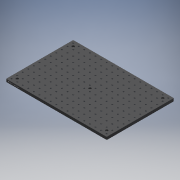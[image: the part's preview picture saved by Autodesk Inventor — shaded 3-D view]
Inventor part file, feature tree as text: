
AUTODESK INVENTOR PART (.ipt)
format: ipt  version: 2019 (Build 230136000, 136)  size: 886,272 bytes
history: mixed  units: in
note: dims shown in document units (in); Inventor stores cm internally (conversion verified against a paired STEP export)
features: extrude x1, sketch x1, projected_geometry x1, other x1, imported_body x1
ambient origin geometry x8: Origin, YZ Plane, XZ Plane, XY Plane, X Axis, Y Axis, Z Axis, Center Point
bodies: Solid1 (imported_parasolid)
feature tree (5):
  extrude  "Extrusion1"  Depth=0.1969in
  sketch  "Sketch1"  dims[d0=0.1969in d1=0.1969in d2=0.1969in d3=0.1969in d4=2.0in d5=0.0in]
  projected_geometry  "Projected Loop1"
  other  "MB1218 - Aluminium Breadboard 304.8 x 457.2 x 12.7mm-1-solid1"
  imported_body  NMx_Import_Brep_tag  [imported B-rep: ~14 faces, bbox_mm=[453.9, 12.4, 304.5]]
